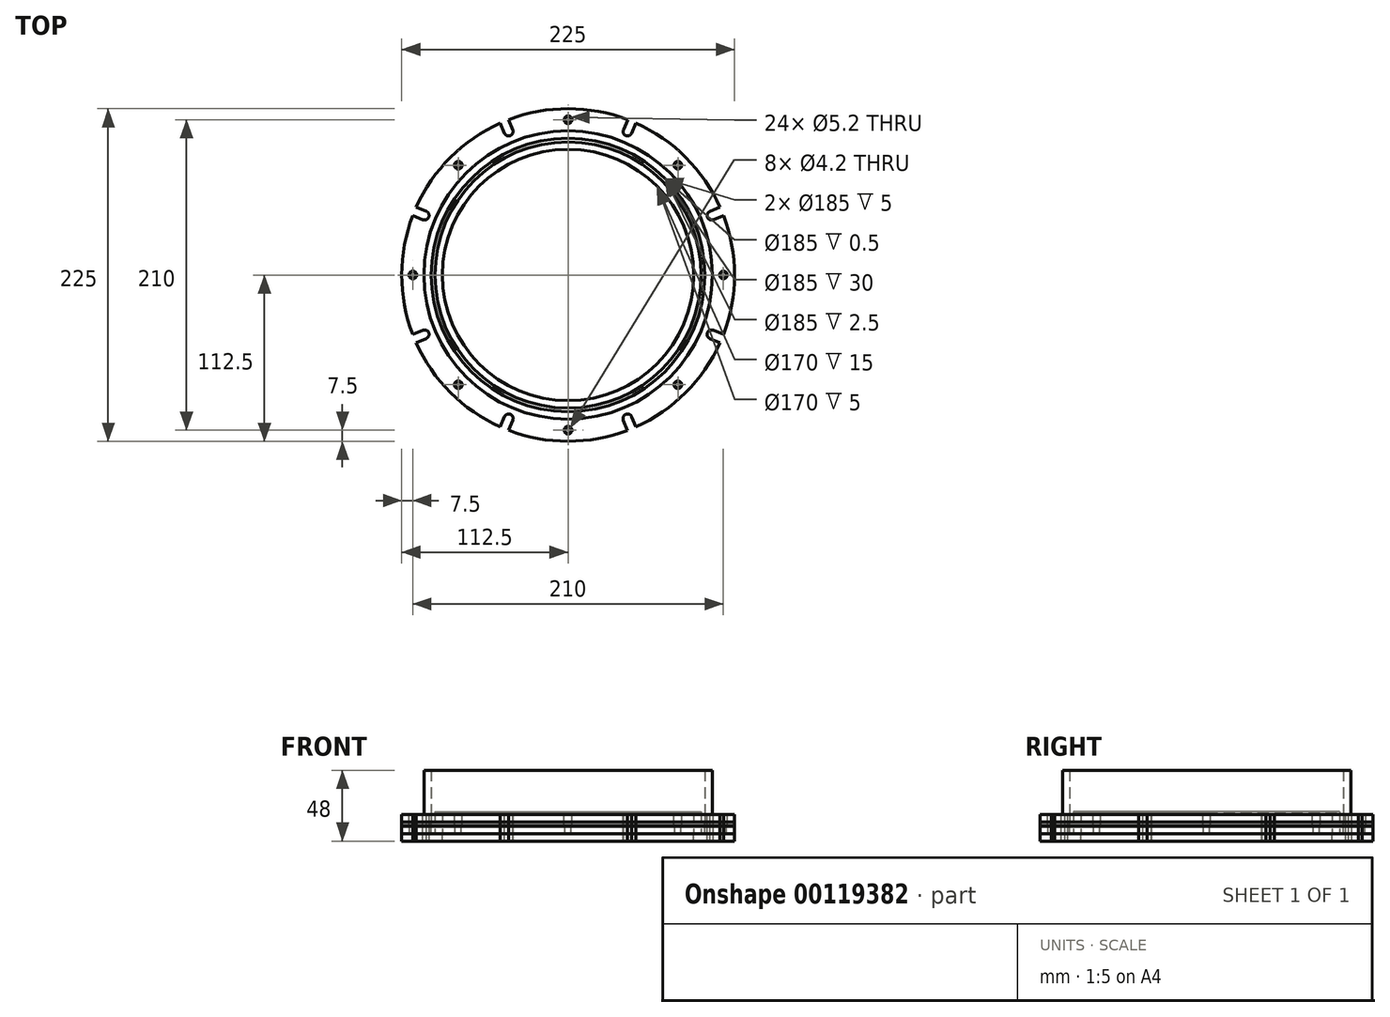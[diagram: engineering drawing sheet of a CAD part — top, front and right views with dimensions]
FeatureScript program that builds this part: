
annotation { "Feature Type Name" : "Feature", "Feature Type Description" : "" }
export const myFeature = defineFeature(function(context is Context, id is Id, definition is map)
    precondition{}
    {
        {
            var Q0;
            Q0=qCreatedBy(makeId("Top.planeOp"),FACE);
            var sketch = newSketch(context, id + "F0", { "sketchPlane" : qUnion([Q0])});
            skCircle(sketch, "E0", {"center": v(0, 0) * mm, "radius": 112.5 * mm});
            skCircle(sketch, "E1", {"center": v(0, 0) * mm, "radius": 92.5 * mm});
            skSolve(sketch);
        }
        {
            var Q0;
            Q0=makeQuery(id+"F0.imprint","IMPRINT",FACE,{"disambiguationData":[TD([[makeQuery(id+"F0.imprint","IMPRINT",EDGE,{"derivedFrom":sQuery(id+"F0.wireOp",EDGE,"E0")}),1.0]])]});
            extrude(context, id + "F1", {"entities" : qUnion([Q0]), "depth" : 5 * mm});
        }
        {
            var Q0;
            Q0=makeQuery(id+"F1.opExtrude","CAP_FACE",FACE,{"disambiguationData":[OSD([sQuery(id+"F0.wireOp",EDGE,"E0"),sQuery(id+"F0.wireOp",EDGE,"E1")])],"isStart":false});
            var sketch = newSketch(context, id + "F2", { "sketchPlane" : qUnion([Q0])});
            skCircle(sketch, "E2.0", {"center": v(0, 0) * mm, "radius": 92.5 * mm});
            skCircle(sketch, "E3", {"center": v(0, 0) * mm, "radius": 97.5 * mm});
            skSolve(sketch);
        }
        {
            var Q0;
            Q0=makeQuery(id+"F2.imprint","IMPRINT",FACE,{"disambiguationData":[TD([[makeQuery(id+"F2.imprint","IMPRINT",EDGE,{"derivedFrom":sQuery(id+"F2.wireOp",EDGE,"E2.0")}),-1.0]])]});
            extrude(context, id + "F3", {"entities" : qUnion([Q0]), "depth" : 30 * mm});
        }
        {
            var Q0;
            Q0=makeQuery(id+"F1.opExtrude","CAP_FACE",FACE,{"disambiguationData":[OSD([sQuery(id+"F0.wireOp",EDGE,"E0"),sQuery(id+"F0.wireOp",EDGE,"E1")])],"isStart":true});
            extrude(context, id + "F4", {"entities" : qUnion([Q0]), "depth" : 2.5 * mm});
        }
        {
            var Q0;
            Q0=makeQuery(id+"F4.opExtrude","CAP_FACE",FACE,{"disambiguationData":[OSD([sQuery(id+"F0.wireOp",EDGE,"E0"),sQuery(id+"F0.wireOp",EDGE,"E1")])],"isStart":false});
            extrude(context, id + "F5", {"entities" : qUnion([Q0]), "depth" : .5 * mm});
        }
        {
            var Q0;
            Q0=makeQuery(id+"F5.opExtrude","CAP_FACE",FACE,{"disambiguationData":[OSD([sQuery(id+"F0.wireOp",EDGE,"E0"),sQuery(id+"F0.wireOp",EDGE,"E1")])],"isStart":false});
            extrude(context, id + "F6", {"entities" : qUnion([Q0]), "depth" : 5 * mm});
        }
        {
            var Q0;
            Q0=makeQuery(id+"F6.opExtrude","CAP_FACE",FACE,{"disambiguationData":[OSD([sQuery(id+"F0.wireOp",EDGE,"E0"),sQuery(id+"F0.wireOp",EDGE,"E1")])],"isStart":false});
            var sketch = newSketch(context, id + "F7", { "sketchPlane" : qUnion([Q0])});
            skCircle(sketch, "E4", {"center": v(0, 0) * mm, "radius": 112.5 * mm});
            skCircle(sketch, "E5", {"center": v(0, 0) * mm, "radius": 85 * mm});
            skSolve(sketch);
        }
        {
            var Q0;
            Q0=makeQuery(id+"F7.imprint","IMPRINT",FACE,{"disambiguationData":[TD([[makeQuery(id+"F7.imprint","IMPRINT",EDGE,{"derivedFrom":sQuery(id+"F7.wireOp",EDGE,"E4")}),-1.0]])]});
            var Q1;
            Q1=makeQuery(id+"F7.imprint","IMPRINT",FACE,{"disambiguationData":[TD([[makeQuery(id+"F7.imprint","IMPRINT",EDGE,{"derivedFrom":sQuery(id+"F7.wireOp",EDGE,"E5")}),-1.0]])]});
            extrude(context, id + "F8", {"entities" : qUnion([Q0, Q1]), "depth" : 5 * mm});
        }
        {
            var Q0;
            Q0=makeQuery(id+"F1.opExtrude","CAP_FACE",FACE,{"disambiguationData":[OSD([sQuery(id+"F0.wireOp",EDGE,"E0"),sQuery(id+"F0.wireOp",EDGE,"E1")])],"isStart":false});
            var sketch = newSketch(context, id + "F9", { "sketchPlane" : qUnion([Q0])});
            skCircle(sketch, "E6", {"center": v(0, 0) * mm, "radius": 105 * mm, "construction": true});
            skPoint(sketch, "E7", {"position": v(0, -105) * mm});
            skPoint(sketch, "E8.1.0", {"position": v(40.18, -97) * mm});
            skPoint(sketch, "E8.2.0", {"position": v(74.25, -74.25) * mm});
            skPoint(sketch, "E8.3.0", {"position": v(97, -40.18) * mm});
            skPoint(sketch, "E8.4.0", {"position": v(105, 0) * mm});
            skPoint(sketch, "E8.5.0", {"position": v(97, 40.18) * mm});
            skPoint(sketch, "E8.6.0", {"position": v(74.25, 74.25) * mm});
            skPoint(sketch, "E8.7.0", {"position": v(40.18, 97) * mm});
            skPoint(sketch, "E8.8.0", {"position": v(0, 105) * mm});
            skPoint(sketch, "E8.9.0", {"position": v(-40.18, 97) * mm});
            skPoint(sketch, "E8.10.0", {"position": v(-74.25, 74.25) * mm});
            skPoint(sketch, "E8.11.0", {"position": v(-97, 40.18) * mm});
            skPoint(sketch, "E8.12.0", {"position": v(-105, 0) * mm});
            skPoint(sketch, "E8.13.0", {"position": v(-97, -40.18) * mm});
            skPoint(sketch, "E8.14.0", {"position": v(-74.25, -74.25) * mm});
            skPoint(sketch, "E8.15.0", {"position": v(-40.18, -97) * mm});
            skSolve(sketch);
        }
        {
            var Q0;
            Q0=sQuery(id+"F9.wireOp",VERTEX,"E7");
            var Q1;
            Q1=sQuery(id+"F9.wireOp",VERTEX,"E8.14.0");
            var Q2;
            Q2=sQuery(id+"F9.wireOp",VERTEX,"E8.12.0");
            var Q3;
            Q3=sQuery(id+"F9.wireOp",VERTEX,"E8.10.0");
            var Q4;
            Q4=sQuery(id+"F9.wireOp",VERTEX,"E8.8.0");
            var Q5;
            Q5=sQuery(id+"F9.wireOp",VERTEX,"E8.6.0");
            var Q6;
            Q6=sQuery(id+"F9.wireOp",VERTEX,"E8.4.0");
            var Q7;
            Q7=sQuery(id+"F9.wireOp",VERTEX,"E8.2.0");
            var Q8;
            Q8=makeQuery(id+"F1.opExtrude","SWEPT_BODY",BODY,{"disambiguationData":[OSD([sQuery(id+"F0.wireOp",EDGE,"E0"),sQuery(id+"F0.wireOp",EDGE,"E1")])]});
            var Q9;
            Q9=makeQuery(id+"F4.opExtrude","SWEPT_BODY",BODY,{"disambiguationData":[OSD([sQuery(id+"F0.wireOp",EDGE,"E0"),sQuery(id+"F0.wireOp",EDGE,"E1")])]});
            var Q10;
            Q10=makeQuery(id+"F5.opExtrude","SWEPT_BODY",BODY,{"disambiguationData":[OSD([sQuery(id+"F0.wireOp",EDGE,"E0"),sQuery(id+"F0.wireOp",EDGE,"E1")])]});
            hole(context, id + "F10", {"style" : HoleStyle.SIMPLE, "endStyle" : HoleEndStyle.THROUGH, "holeDiameter" : 5.2 * mm, "locations" : qUnion([Q0, Q1, Q2, Q3, Q4, Q5, Q6, Q7]), "scope" : qUnion([Q8, Q9, Q10]), "isTappedThrough" : true});
        }
        {
            var Q0;
            Q0=sQuery(id+"F9.wireOp",VERTEX,"E8.12.0");
            var Q1;
            Q1=sQuery(id+"F9.wireOp",VERTEX,"E8.10.0");
            var Q2;
            Q2=sQuery(id+"F9.wireOp",VERTEX,"E8.8.0");
            var Q3;
            Q3=sQuery(id+"F9.wireOp",VERTEX,"E8.6.0");
            var Q4;
            Q4=sQuery(id+"F9.wireOp",VERTEX,"E8.4.0");
            var Q5;
            Q5=sQuery(id+"F9.wireOp",VERTEX,"E8.2.0");
            var Q6;
            Q6=sQuery(id+"F9.wireOp",VERTEX,"E7");
            var Q7;
            Q7=sQuery(id+"F9.wireOp",VERTEX,"E8.14.0");
            var Q8;
            Q8=makeQuery(id+"F6.opExtrude","SWEPT_BODY",BODY,{"disambiguationData":[OSD([sQuery(id+"F0.wireOp",EDGE,"E0"),sQuery(id+"F0.wireOp",EDGE,"E1")])]});
            hole(context, id + "F11", {"style" : HoleStyle.SIMPLE, "endStyle" : HoleEndStyle.THROUGH, "holeDiameter" : 4.2 * mm, "locations" : qUnion([Q0, Q1, Q2, Q3, Q4, Q5, Q6, Q7]), "scope" : qUnion([Q8]), "isTappedThrough" : true});
        }
        {
            var Q0;
            Q0=makeQuery(id+"F9.imprint","IMPRINT",FACE,{"disambiguationData":[TD([[makeQuery(id+"F9.imprint","IMPRINT",EDGE,{"derivedFrom":makeQuery(id+"F1.opExtrude","CAP_EDGE",EDGE,{"disambiguationData":[OSD([sQuery(id+"F0.wireOp",EDGE,"E1")])],"isStart":false})}),1.0]])]});
            var sketch = newSketch(context, id + "F12", { "sketchPlane" : qUnion([Q0])});
            skLineSegment(sketch, "E9", {"start": v(0, 0) * mm, "end": v(-46.6, 112.48) * mm, "construction": true});
            skCircle(sketch, "E10", {"center": v(0, 0) * mm, "radius": 105 * mm, "construction": true});
            skArc(sketch, "E11", {"start": v(-42.97, 95.9) * mm, "mid": v(-39.07, 94.22) * mm, "end": v(-37.4, 98.12) * mm});
            skLineSegment(sketch, "E12", {"start": v(-42.94, 95.82) * mm, "end": v(-48.68, 109.68) * mm});
            skLineSegment(sketch, "E13", {"start": v(-37.4, 98.12) * mm, "end": v(-43.47, 113.4) * mm});
            skLineSegment(sketch, "E14", {"start": v(-43.47, 113.4) * mm, "end": v(-48.68, 109.68) * mm});
            skLineSegment(sketch, "E15.1.0", {"start": v(-95.82, 42.94) * mm, "end": v(-110.92, 49.44) * mm});
            skLineSegment(sketch, "E15.1.1", {"start": v(-110.92, 49.44) * mm, "end": v(-111.97, 43.13) * mm});
            skArc(sketch, "E15.1.2", {"start": v(-98.2, 37.43) * mm, "mid": v(-94.25, 39) * mm, "end": v(-95.82, 42.94) * mm});
            skLineSegment(sketch, "E15.1.3", {"start": v(-98.12, 37.4) * mm, "end": v(-111.97, 43.13) * mm});
            skLineSegment(sketch, "E15.2.0", {"start": v(-98.12, -37.4) * mm, "end": v(-113.4, -43.47) * mm});
            skLineSegment(sketch, "E15.2.1", {"start": v(-113.4, -43.47) * mm, "end": v(-109.68, -48.68) * mm});
            skArc(sketch, "E15.2.2", {"start": v(-95.9, -42.97) * mm, "mid": v(-94.22, -39.07) * mm, "end": v(-98.12, -37.4) * mm});
            skLineSegment(sketch, "E15.2.3", {"start": v(-95.82, -42.94) * mm, "end": v(-109.68, -48.68) * mm});
            skLineSegment(sketch, "E15.3.0", {"start": v(-42.94, -95.82) * mm, "end": v(-49.44, -110.92) * mm});
            skLineSegment(sketch, "E15.3.1", {"start": v(-49.44, -110.92) * mm, "end": v(-43.13, -111.97) * mm});
            skArc(sketch, "E15.3.2", {"start": v(-37.43, -98.2) * mm, "mid": v(-39, -94.25) * mm, "end": v(-42.94, -95.82) * mm});
            skLineSegment(sketch, "E15.3.3", {"start": v(-37.4, -98.12) * mm, "end": v(-43.13, -111.97) * mm});
            skLineSegment(sketch, "E15.4.0", {"start": v(37.4, -98.12) * mm, "end": v(43.47, -113.4) * mm});
            skLineSegment(sketch, "E15.4.1", {"start": v(43.47, -113.4) * mm, "end": v(48.68, -109.68) * mm});
            skArc(sketch, "E15.4.2", {"start": v(42.97, -95.9) * mm, "mid": v(39.07, -94.22) * mm, "end": v(37.4, -98.12) * mm});
            skLineSegment(sketch, "E15.4.3", {"start": v(42.94, -95.82) * mm, "end": v(48.68, -109.68) * mm});
            skLineSegment(sketch, "E15.5.0", {"start": v(95.82, -42.94) * mm, "end": v(110.92, -49.44) * mm});
            skLineSegment(sketch, "E15.5.1", {"start": v(110.92, -49.44) * mm, "end": v(111.97, -43.13) * mm});
            skArc(sketch, "E15.5.2", {"start": v(98.2, -37.43) * mm, "mid": v(94.25, -39) * mm, "end": v(95.82, -42.94) * mm});
            skLineSegment(sketch, "E15.5.3", {"start": v(98.12, -37.4) * mm, "end": v(111.97, -43.13) * mm});
            skLineSegment(sketch, "E15.6.0", {"start": v(98.12, 37.4) * mm, "end": v(113.4, 43.47) * mm});
            skLineSegment(sketch, "E15.6.1", {"start": v(113.4, 43.47) * mm, "end": v(109.68, 48.68) * mm});
            skArc(sketch, "E15.6.2", {"start": v(95.9, 42.97) * mm, "mid": v(94.22, 39.07) * mm, "end": v(98.12, 37.4) * mm});
            skLineSegment(sketch, "E15.6.3", {"start": v(95.82, 42.94) * mm, "end": v(109.68, 48.68) * mm});
            skLineSegment(sketch, "E15.7.0", {"start": v(42.94, 95.82) * mm, "end": v(49.44, 110.92) * mm});
            skLineSegment(sketch, "E15.7.1", {"start": v(49.44, 110.92) * mm, "end": v(43.13, 111.97) * mm});
            skArc(sketch, "E15.7.2", {"start": v(37.43, 98.2) * mm, "mid": v(39, 94.25) * mm, "end": v(42.94, 95.82) * mm});
            skLineSegment(sketch, "E15.7.3", {"start": v(37.4, 98.12) * mm, "end": v(43.13, 111.97) * mm});
            skSolve(sketch);
        }
        {
            var Q0;
            Q0 = qSketchRegion(id + "F12", true);
            extrude(context, id + "F13", {"entities" : qUnion([Q0]), "operationType" : NewBodyOperationType.REMOVE, "endBound" : BoundingType.THROUGH_ALL, "oppositeDirection" : true, "depth" : 25 * mm});
        }
        {
            var Q0;
            Q0=makeQuery(id+"F7.imprint","IMPRINT",FACE,{"disambiguationData":[TD([[makeQuery(id+"F7.imprint","IMPRINT",EDGE,{"derivedFrom":sQuery(id+"F7.wireOp",EDGE,"E4")}),-1.0]])]});
            var sketch = newSketch(context, id + "F14", { "sketchPlane" : qUnion([Q0])});
            skCircle(sketch, "E16", {"center": v(0, 0) * mm, "radius": 85 * mm});
            skCircle(sketch, "E17", {"center": v(0, 0) * mm, "radius": 90 * mm});
            skSolve(sketch);
        }
        {
            var Q0;
            Q0 = qSketchRegion(id + "F14", true);
            extrude(context, id + "F15", {"entities" : qUnion([Q0]), "oppositeDirection" : true, "depth" : 15 * mm});
        }
    });
